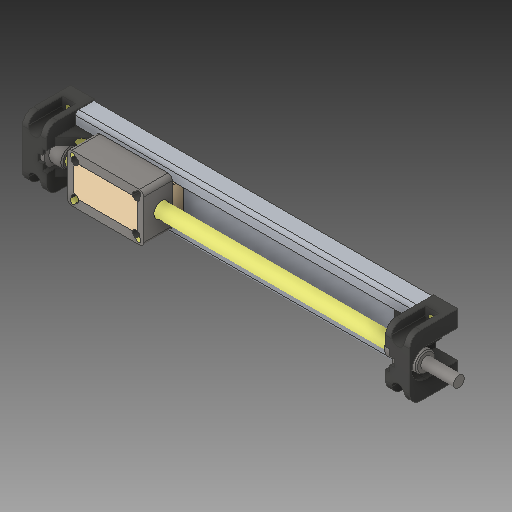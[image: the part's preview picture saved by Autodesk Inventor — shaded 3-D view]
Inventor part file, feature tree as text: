
AUTODESK INVENTOR PART (.ipt)
format: ipt  version: 2019 (Build 230136000, 136)  size: 434,176 bytes
history: native  units: mm
features: extrude x1, sketch x1
ambient origin geometry x8: Origin, YZ Plane, XZ Plane, XY Plane, X Axis, Y Axis, Z Axis, Center Point
bodies: Solid1 (feature_tree), Solid2 (feature_tree)
feature tree (2):
  extrude  "Extrusion1"  Depth=10.0mm
  sketch  "Sketch1"  dims[d0=28.0mm d1=15.0mm d2=3.5mm d3=3.5mm d4=3.5mm d5=3.5mm d6=10.0mm d7=0.0mm]
